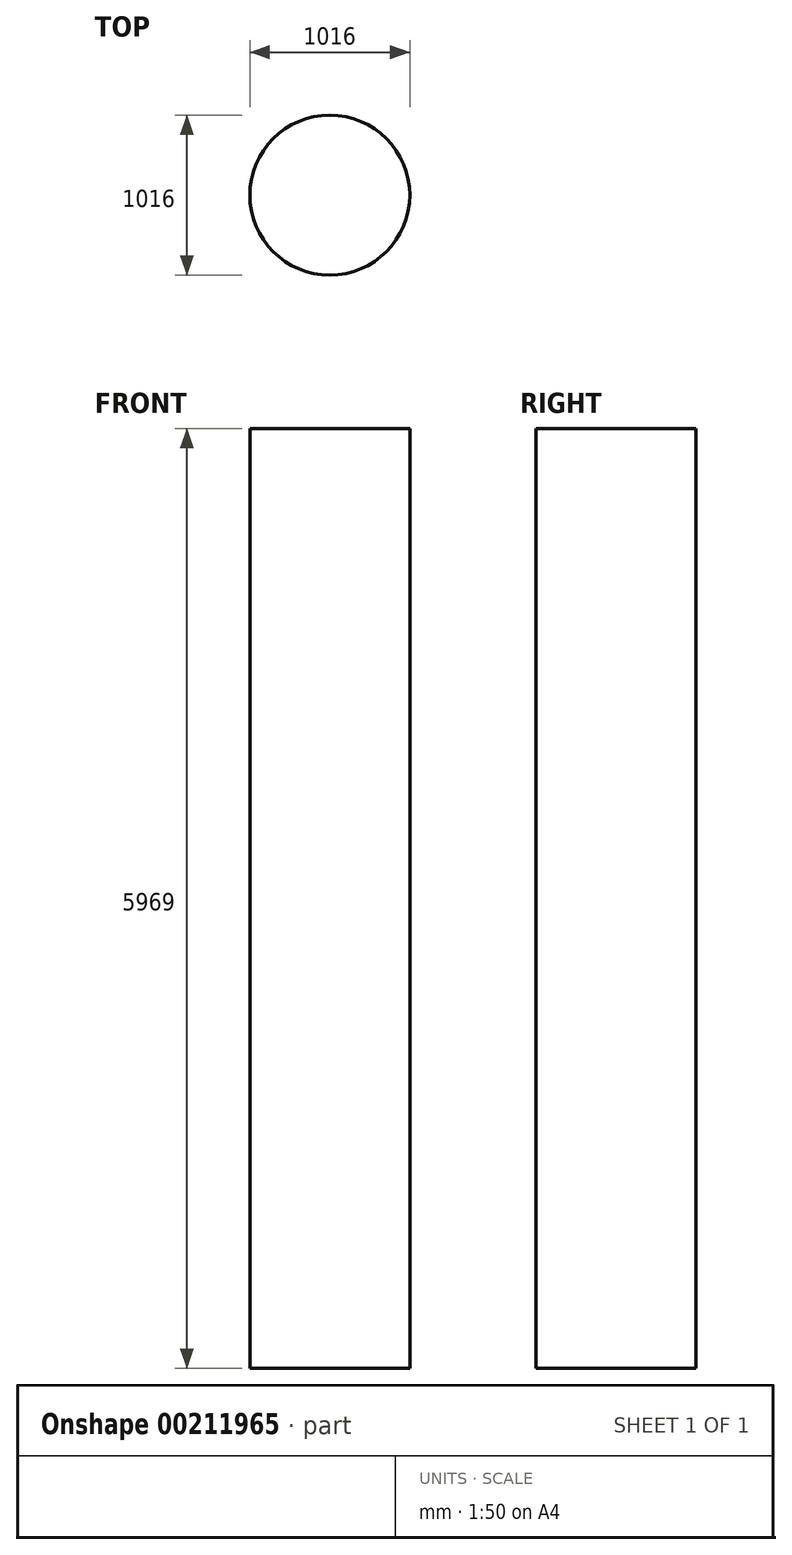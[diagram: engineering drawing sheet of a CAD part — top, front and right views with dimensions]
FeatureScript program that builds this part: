
annotation { "Feature Type Name" : "Feature", "Feature Type Description" : "" }
export const myFeature = defineFeature(function(context is Context, id is Id, definition is map)
    precondition{}
    {
        {
            var Q0;
            Q0=qCreatedBy(makeId("Top.planeOp"),FACE);
            var sketch = newSketch(context, id + "F0", { "sketchPlane" : qUnion([Q0])});
            skCircle(sketch, "E0", {"center": v(0, 0) * mm, "radius": 508 * mm});
            skSolve(sketch);
        }
        {
            var Q0;
            Q0=makeQuery(id+"F0.imprint","IMPRINT",FACE,{"disambiguationData":[TD([[makeQuery(id+"F0.imprint","IMPRINT",EDGE,{"derivedFrom":sQuery(id+"F0.wireOp",EDGE,"E0")}),1.0]])]});
            extrude(context, id + "F1", {"entities" : qUnion([Q0]), "depth" : 5969 * mm});
        }
    });
